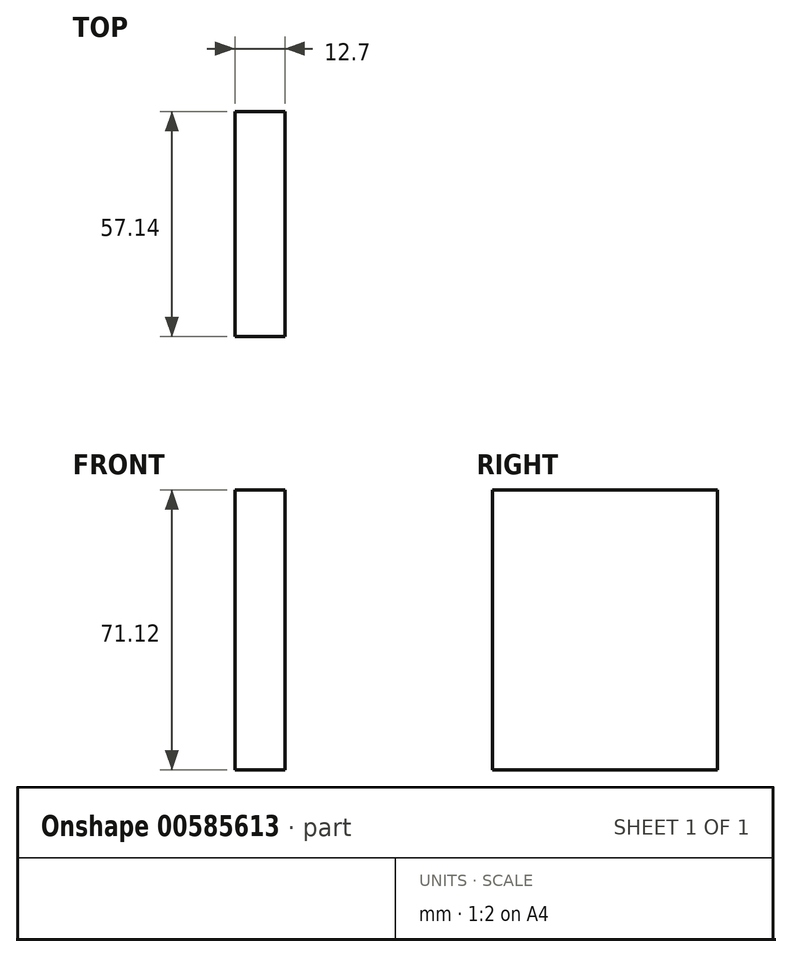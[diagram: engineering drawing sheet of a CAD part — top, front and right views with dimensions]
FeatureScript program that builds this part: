
annotation { "Feature Type Name" : "Feature", "Feature Type Description" : "" }
export const myFeature = defineFeature(function(context is Context, id is Id, definition is map)
    precondition{}
    {
        {
            var Q0;
            Q0=qCreatedBy(makeId("Top.planeOp"),FACE);
            var sketch = newSketch(context, id + "F0", { "sketchPlane" : qUnion([Q0])});
            skLineSegment(sketch, "E0.bottom", {"start": v(-6.35, -28.58) * mm, "end": v(6.35, -28.58) * mm});
            skLineSegment(sketch, "E0.top", {"start": v(-6.35, 28.58) * mm, "end": v(6.35, 28.58) * mm});
            skLineSegment(sketch, "E0.left", {"start": v(-6.35, -28.58) * mm, "end": v(-6.35, 28.58) * mm});
            skLineSegment(sketch, "E0.right", {"start": v(6.35, -28.58) * mm, "end": v(6.35, 28.58) * mm});
            skPoint(sketch, "E0.middle", {"position": v(0, 0) * mm});
            skSolve(sketch);
        }
        {
            var Q0;
            Q0=makeQuery(id+"F0.imprint","IMPRINT",FACE,{"disambiguationData":[TD([[makeQuery(id+"F0.imprint","IMPRINT",EDGE,{"derivedFrom":sQuery(id+"F0.wireOp",EDGE,"E0.bottom")}),1.0]])]});
            extrude(context, id + "F1", {"entities" : qUnion([Q0]), "depth" : 71.12 * mm, "offsetDistance" : 25.4 * mm});
        }
    });
